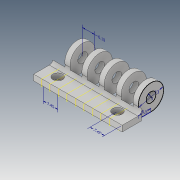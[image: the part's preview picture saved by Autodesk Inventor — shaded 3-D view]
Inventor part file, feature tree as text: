
AUTODESK INVENTOR PART (.ipt)
format: ipt  version: 2019 (Build 230136000, 136)  size: 221,184 bytes
history: native  units: mm
features: plane x10, extrude x8, other x4, sketch x4, fillet x2, projected_geometry x1
ambient origin geometry x8: Origin, YZ Plane, XZ Plane, XY Plane, X Axis, Y Axis, Z Axis, Center Point
bodies: Solid1 (feature_tree)
feature tree (29):
  other  "Annotations"
  extrude  "Extrusion1"  Depth=3.0mm TaperAngle=0.0deg
  extrude  "Extrusion2"  Depth=3.0mm TaperAngle=0.0deg
  sketch  "Sketch3"  dims[d18=5.0mm d19=5.0mm]
  plane  "Work Plane8"
  plane  "Work Plane9"
  extrude  "Extrusion8"  Depth=5.0mm
  extrude  "Extrusion9"  Depth=6.1mm
  extrude  "Extrusion10"  Depth=6.1mm
  extrude  "Extrusion11"  [1 undecoded]
  extrude  "Extrusion12"  [1 undecoded]
  fillet  "Fillet1"  [1 undecoded]
  fillet  "Fillet2"  [1 undecoded]
  plane  "Work Plane12"
  extrude  "Extrusion13"  [1 undecoded]
  sketch  "Sketch1"  dims[d0=44.0mm d6=10.0mm d7=3.0mm d8=0.0mm]
  sketch  "Sketch2"  dims[d9=5.0mm d10=5.0mm d14=30.8mm d16=3.0mm d17=0.0mm]
  plane  "Work Plane1"
  plane  "Work Plane2"
  plane  "Work Plane3"
  plane  "Work Plane4"
  plane  "Work Plane5"
  plane  "Work Plane6"
  plane  "Work Plane7"
  sketch  "Sketch4"  dims[d20=6.5mm d22=13.0mm d23=5.0mm d24=-4.4mm d25=-4.4mm d26=-4.4mm d27=-4.4mm d28=-4.4mm d29=-4.4mm d30=-4.4mm d31=-4.4mm d41=-4.4mm d45=2.7mm d46=0.0mm d47=2.7mm d48=0.0mm d49=2.7mm d50=0.0mm d51=2.7mm d52=0.0mm d53=2.7mm d54=0.0mm d55=2.0mm d56=2.0mm d58=1.7mm d59=0.0mm d60=7.45mm d57=6.1mm d61=1.624677mm d62=7.45mm d63=2.432498mm d64=7.45mm]
  projected_geometry  "Projected Loop1"
  other  "Linear Dimension 1"
  other  "Linear Dimension 2"
  other  "Linear Dimension 3"
note: 5 required parameter values undecoded (feature->parameter linkage not recoverable at this tier; creation-order binding heuristic only, values carry confidence <= 0.55)
